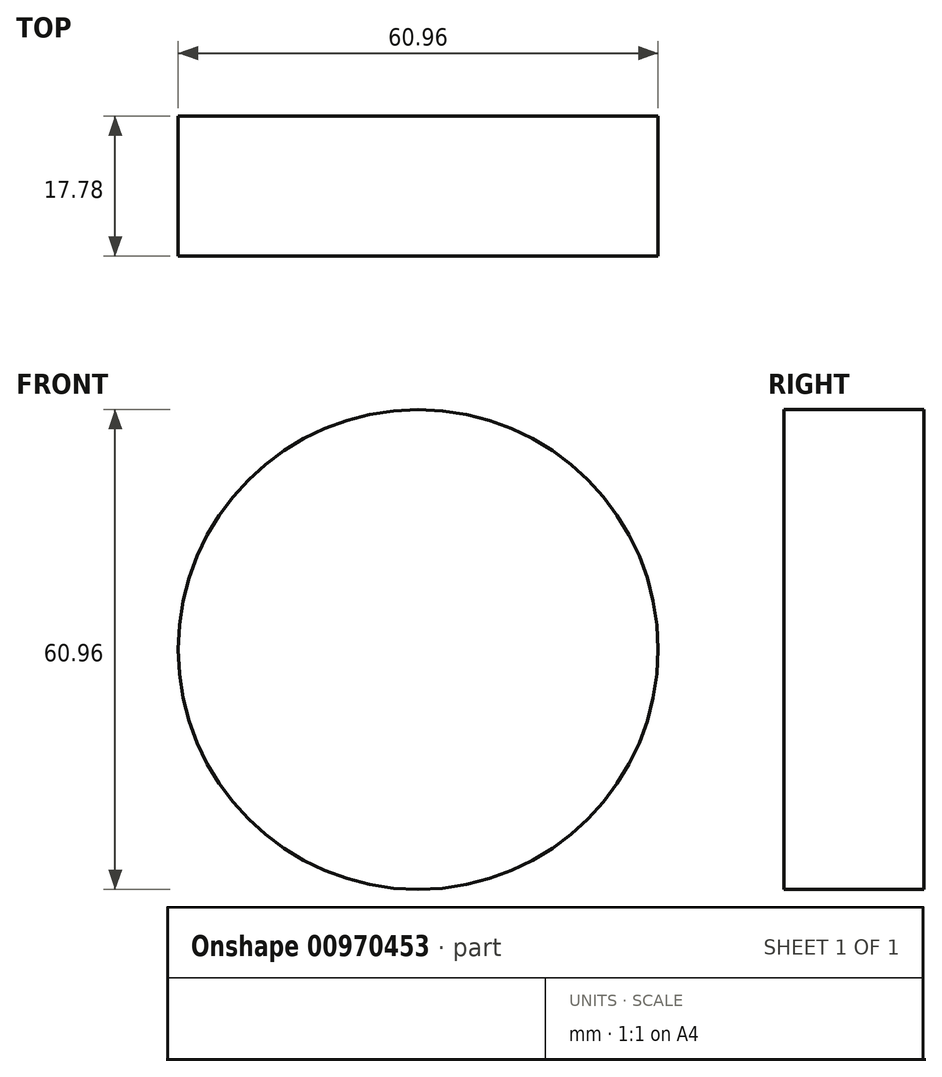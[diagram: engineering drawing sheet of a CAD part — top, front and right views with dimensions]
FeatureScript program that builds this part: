
annotation { "Feature Type Name" : "Feature", "Feature Type Description" : "" }
export const myFeature = defineFeature(function(context is Context, id is Id, definition is map)
    precondition{}
    {
        {
            var Q0;
            Q0=qCreatedBy(makeId("Front.planeOp"), FACE);
            var sketch = newSketch(context, id + "F0", { "sketchPlane" : qUnion([Q0])});
            skCircle(sketch, "E0", {"center": v(0, 0) * mm, "radius": 30.48 * mm});
            skSolve(sketch);
        }
        {
            var Q0;
            Q0 = qSketchRegion(id + "F0", true);
            extrude(context, id + "F1", {"entities" : qUnion([Q0]), "domain" : OperationDomain.MODEL, "flatOperationType" : FlatOperationType.REMOVE, "oppositeDirection" : true, "depth" : 17.78 * mm, "offsetDistance" : 25 * mm});
        }
    });
